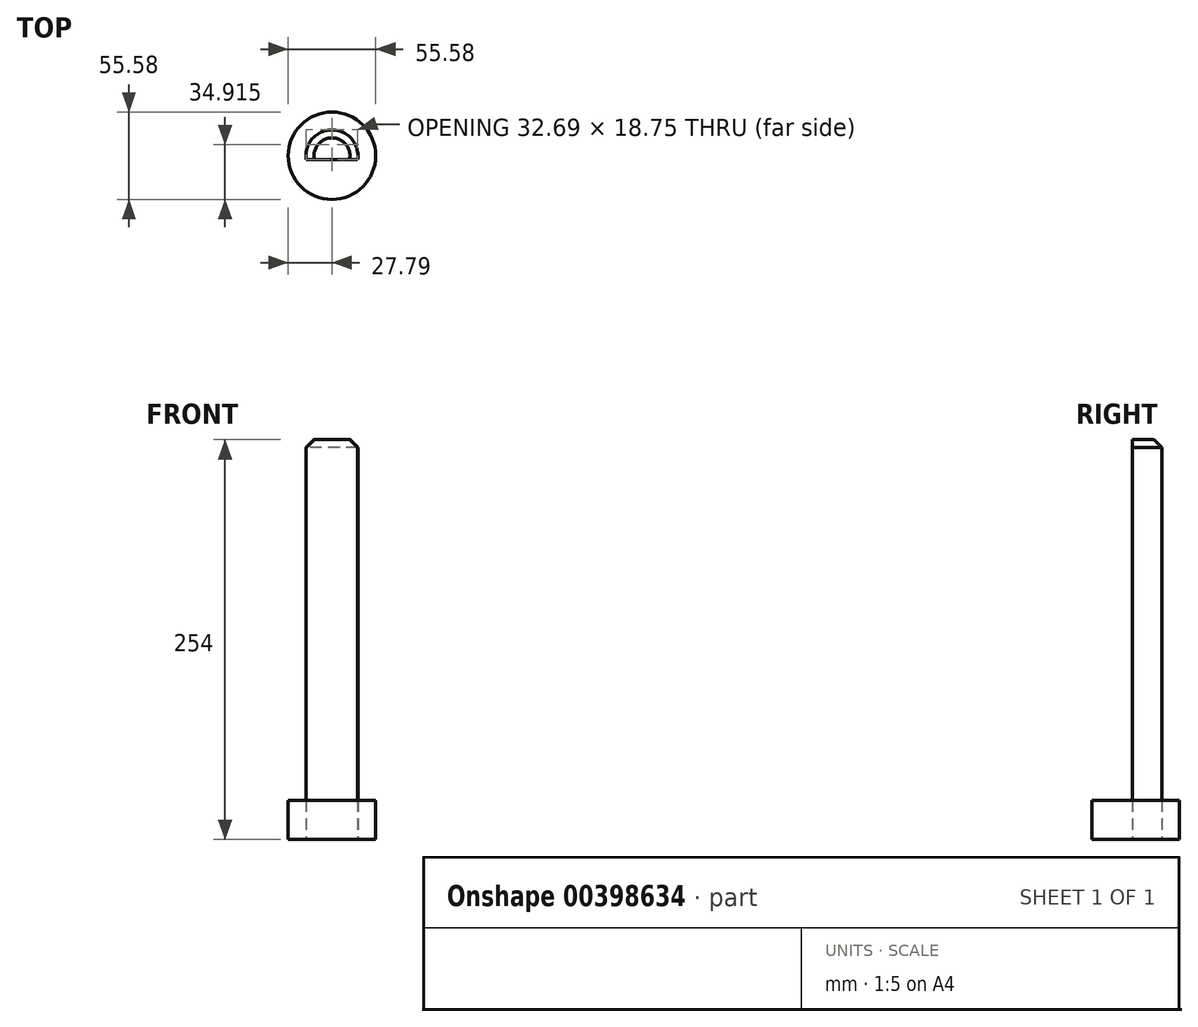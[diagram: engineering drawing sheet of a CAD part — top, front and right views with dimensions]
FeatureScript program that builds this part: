
annotation { "Feature Type Name" : "Feature", "Feature Type Description" : "" }
export const myFeature = defineFeature(function(context is Context, id is Id, definition is map)
    precondition{}
    {
        {
            var Q0;
            Q0=qCreatedBy(makeId("Top.planeOp"),FACE);
            var sketch = newSketch(context, id + "F0", { "sketchPlane" : qUnion([Q0])});
            skArc(sketch, "E0", {"start": v(16.35, -2.25) * mm, "mid": v(0, 16.5) * mm, "end": v(-16.35, -2.25) * mm});
            skLineSegment(sketch, "E1", {"start": v(-16.35, -2.25) * mm, "end": v(-16.35, 0) * mm, "construction": true});
            skLineSegment(sketch, "E2", {"start": v(16.35, -2.25) * mm, "end": v(16.35, 0) * mm, "construction": true});
            skLineSegment(sketch, "E3", {"start": v(-16.35, -2.25) * mm, "end": v(16.35, -2.25) * mm});
            skSolve(sketch);
        }
        {
            var Q0;
            Q0=makeQuery(id+"F0.imprint","IMPRINT",FACE,{"disambiguationData":[TD([[makeQuery(id+"F0.imprint","IMPRINT",EDGE,{"derivedFrom":sQuery(id+"F0.wireOp",EDGE,"E0")}),1.0]])]});
            extrude(context, id + "F1", {"entities" : qUnion([Q0]), "depth" : 254 * mm});
        }
        {
            var Q0;
            Q0=makeQuery(id+"F1.opExtrude","CAP_EDGE",EDGE,{"disambiguationData":[OSD([sQuery(id+"F0.wireOp",EDGE,"E0")])],"isStart":false});
            chamfer(context, id + "F2", {"entities" : qUnion([Q0]), "width" : 5.08 * mm, "tangentPropagation" : true});
        }
        {
            var Q0;
            Q0=makeQuery(id+"F1.opExtrude","CAP_FACE",FACE,{"disambiguationData":[OSD([sQuery(id+"F0.wireOp",EDGE,"E0"),sQuery(id+"F0.wireOp",EDGE,"E3")])],"isStart":true});
            var sketch = newSketch(context, id + "F3", { "sketchPlane" : qUnion([Q0])});
            skCircle(sketch, "E4", {"center": v(0, 0) * mm, "radius": 27.8 * mm});
            skSolve(sketch);
        }
        {
            var Q0;
            Q0=makeQuery(id+"F3.imprint","IMPRINT",FACE,{"disambiguationData":[TD([[makeQuery(id+"F3.imprint","IMPRINT",EDGE,{"derivedFrom":sQuery(id+"F3.wireOp",EDGE,"E4")}),1.0]])]});
            extrude(context, id + "F4", {"entities" : qUnion([Q0]), "oppositeDirection" : true, "depth" : 25 * mm});
        }
    });
